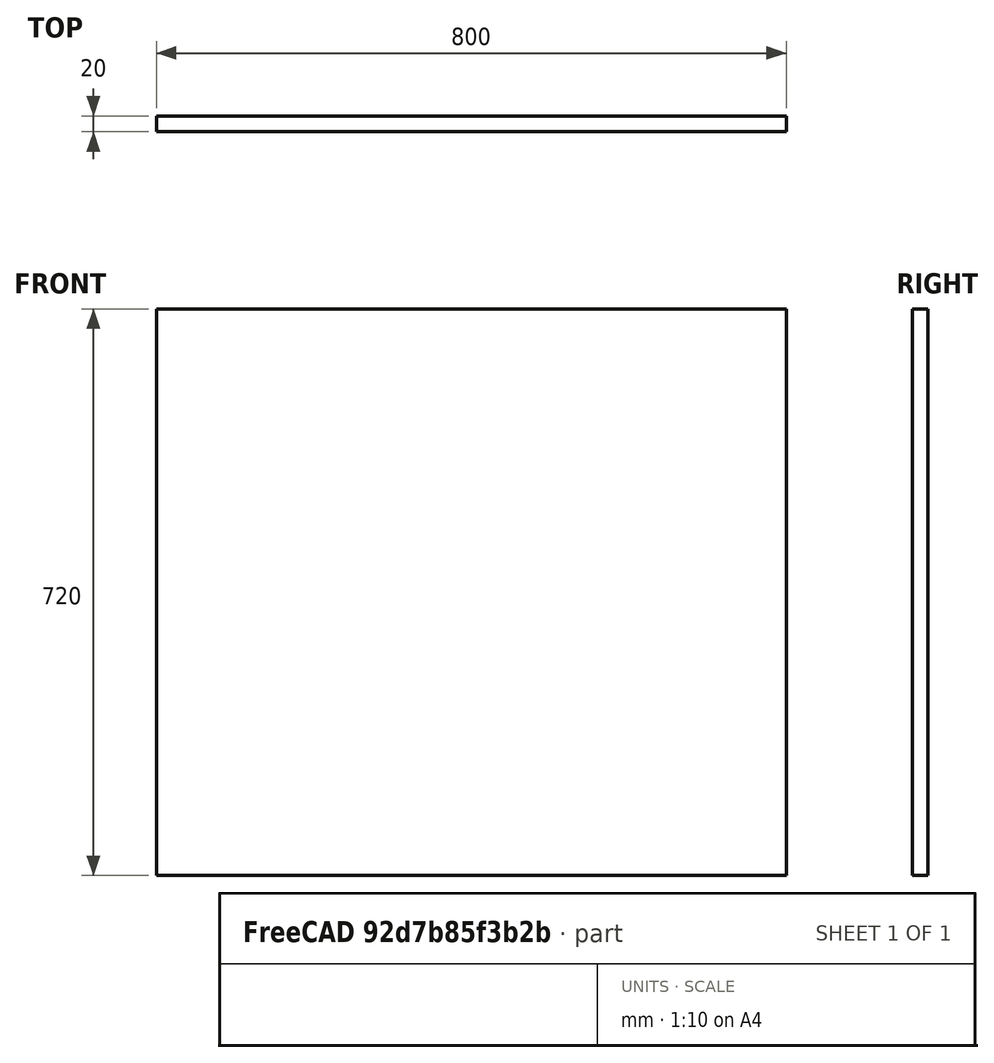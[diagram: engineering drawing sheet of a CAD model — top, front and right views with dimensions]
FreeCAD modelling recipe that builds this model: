
FCSTD DOCUMENT  (FreeCAD 0.20R29603 (Git))
Label: PlatteVorne
License: All rights reserved
LicenseURL: http://en.wikipedia.org/wiki/All_rights_reserved
objects: Sketcher::SketchObject×1, PartDesign::Pad×1, PartDesign::Body×1
note: 4 computed .brp shape members not serialized (recipe doc carries the construction recipe); baked Part::Feature solids carry a one-line shape summary decoded from their .brp

FEATURE [Sketcher::SketchObject] Sketch
  FullyConstrained = true
  MapMode = 5
  Placement = pos=(0,0,0) rot=(1,0,0;1.5708rad)
  Support = -> [XZ_Plane]
  sketch-geometry (5):
    g0: LineSegment StartX=-400 StartY=360 StartZ=0 EndX=-400 EndY=-360 EndZ=0
    g1: LineSegment StartX=-400 StartY=-360 StartZ=0 EndX=400 EndY=-360 EndZ=0
    g2: LineSegment StartX=400 StartY=-360 StartZ=0 EndX=400 EndY=360 EndZ=0
    g3: LineSegment StartX=400 StartY=360 StartZ=0 EndX=-400 EndY=360 EndZ=0
    g4: GeomPoint X=0 Y=0 Z=0
  constraints (12):
    c: Coincident(g0,g1)
    c: Coincident(g1,g2)
    c: Coincident(g2,g3)
    c: Coincident(g3,g0)
    c: Horizontal(g1)
    c: Horizontal(g3)
    c: Vertical(g0)
    c: Vertical(g2)
    c: Symmetric(g1,g0,g4)
    c: Coincident(g4,g-1)
    c: Distance(g1) = 800
    c: Distance(g2) = 720
FEATURE [PartDesign::Pad] Pad
  Direction = (0,-1,-2e-16)
  Length = 20
  Length2 = 10
  Placement = pos=(0,0,0) rot=(1,0,0;1.5708rad)
  Profile = -> Sketch
  ReferenceAxis = -> Sketch [N_Axis]
  Type = 0
FEATURE [PartDesign::Body] Body
  Group = -> [Sketch,Pad]
  Origin = -> Origin
  Tip = -> Pad
